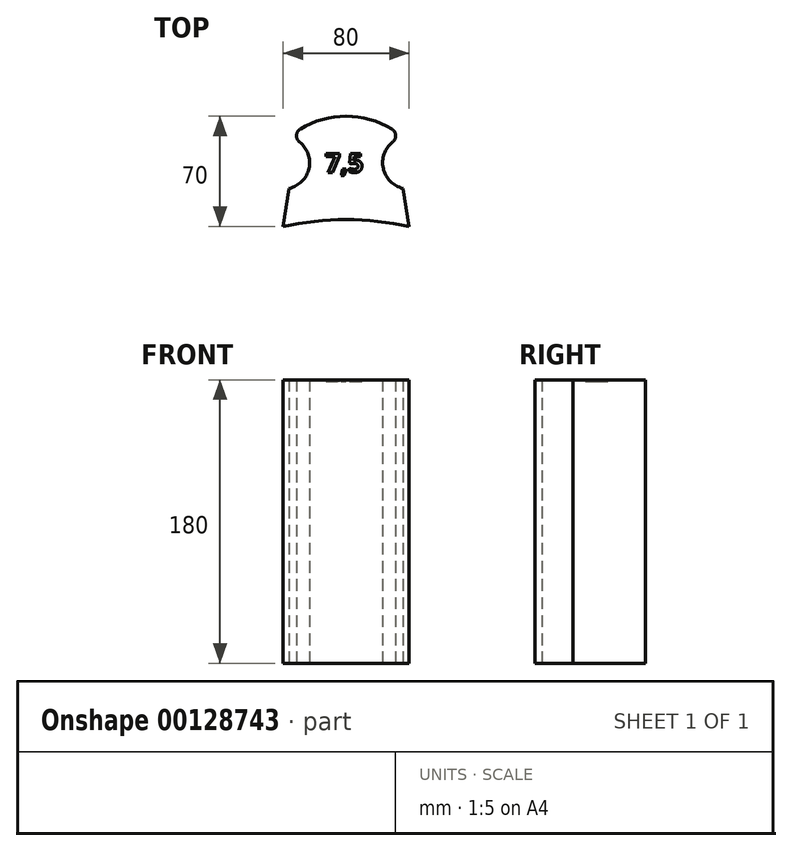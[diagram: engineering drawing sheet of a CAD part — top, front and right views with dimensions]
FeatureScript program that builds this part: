
annotation { "Feature Type Name" : "Feature", "Feature Type Description" : "" }
export const myFeature = defineFeature(function(context is Context, id is Id, definition is map)
    precondition{}
    {
        {
            var Q0;
            Q0=qCreatedBy(makeId("Top.planeOp"),FACE);
            var sketch = newSketch(context, id + "F0", { "sketchPlane" : qUnion([Q0])});
            skLineSegment(sketch, "E0", {"start": v(0, 0) * mm, "end": v(3.87, 24.16) * mm});
            skLineSegment(sketch, "E1", {"start": v(0, 0) * mm, "end": v(80, 0) * mm, "construction": true});
            skLineSegment(sketch, "E2", {"start": v(40, 0) * mm, "end": v(40, 70) * mm, "construction": true});
            skArc(sketch, "E3", {"start": v(3.87, 24.16) * mm, "mid": v(16.4, 36.85) * mm, "end": v(10.4, 53.64) * mm});
            skArc(sketch, "E4.MirrorCS", {"start": v(76.13, 24.16) * mm, "mid": v(63.6, 36.85) * mm, "end": v(69.6, 53.64) * mm});
            skLineSegment(sketch, "E5.MirrorCS", {"start": v(80, 0) * mm, "end": v(76.13, 24.16) * mm});
            skArc(sketch, "E6", {"start": v(69.1, 61.84) * mm, "mid": v(40, 70) * mm, "end": v(10.9, 61.84) * mm});
            skPoint(sketch, "E7.visualSharp", {"position": v(3.87, 56.79) * mm});
            skArc(sketch, "E7.filletArc", {"start": v(10.9, 61.84) * mm, "mid": v(8.5, 57.87) * mm, "end": v(10.4, 53.64) * mm});
            skPoint(sketch, "E8.visualSharp", {"position": v(76.13, 56.79) * mm});
            skArc(sketch, "E8.filletArc", {"start": v(69.6, 53.64) * mm, "mid": v(71.5, 57.87) * mm, "end": v(69.1, 61.84) * mm});
            skArc(sketch, "E9.MirrorCS", {"start": v(0, 0) * mm, "mid": v(40, 4.28) * mm, "end": v(80, 0) * mm});
            skSolve(sketch);
        }
        {
            var Q0;
            Q0=makeQuery(id+"F0.imprint","IMPRINT",FACE,{"disambiguationData":[TD([[makeQuery(id+"F0.imprint","IMPRINT",EDGE,{"derivedFrom":sQuery(id+"F0.wireOp",EDGE,"E0")}),-1.0]])]});
            extrude(context, id + "F1", {"entities" : qUnion([Q0]), "depth" : 180 * mm});
        }
        {
            var Q0;
            Q0=makeQuery(id+"F1.opExtrude","CAP_FACE",FACE,{"disambiguationData":[OSD([sQuery(id+"F0.wireOp",EDGE,"E0"),sQuery(id+"F0.wireOp",EDGE,"E3"),sQuery(id+"F0.wireOp",EDGE,"E4.MirrorCS"),sQuery(id+"F0.wireOp",EDGE,"E5.MirrorCS"),sQuery(id+"F0.wireOp",EDGE,"E6"),sQuery(id+"F0.wireOp",EDGE,"E7.filletArc"),sQuery(id+"F0.wireOp",EDGE,"E8.filletArc"),sQuery(id+"F0.wireOp",EDGE,"NzHJaS1e-Hx9R-e02U-jfAq-aO6yktXq1YBm")])],"isStart":false});
            var sketch = newSketch(context, id + "F2", { "sketchPlane" : qUnion([Q0])});
            skText(sketch, "E10", { "text": "7,5", "fontName": "OpenSans-Bold.ttf"});
            skPoint(sketch, "E11", {"position": v(40, 70) * mm});
            const initialGuessF2  = {"E10": [0.02669, 0.03435, 1, 0, 0.01214]};
            skSetInitialGuess(sketch, initialGuessF2);
            skSolve(sketch);
        }
        {
            var Q0;
            Q0=qSketchRegion(id+"F2",true);
            extrude(context, id + "F3", {"entities" : qUnion([Q0]), "operationType" : NewBodyOperationType.REMOVE, "oppositeDirection" : true, "depth" : 1 * mm});
        }
    });
